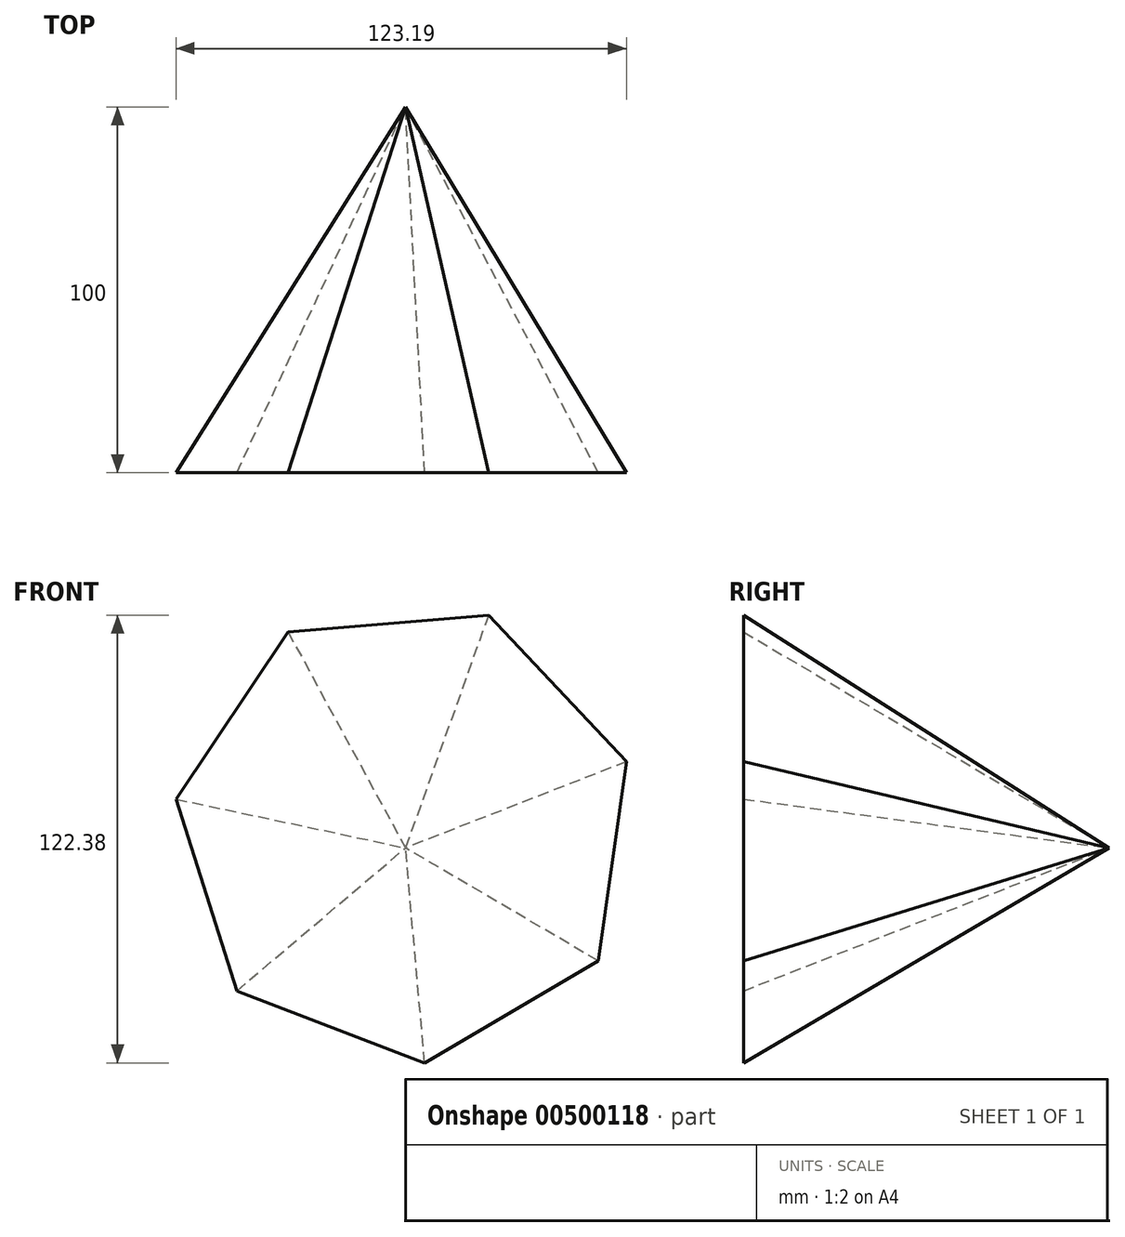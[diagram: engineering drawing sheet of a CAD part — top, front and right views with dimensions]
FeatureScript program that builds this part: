
annotation { "Feature Type Name" : "Feature", "Feature Type Description" : "" }
export const myFeature = defineFeature(function(context is Context, id is Id, definition is map)
    precondition{}
    {
        {
            var Q0;
            Q0=qCreatedBy(makeId("Front.planeOp"),FACE);
            var sketch = newSketch(context, id + "F0", { "sketchPlane" : qUnion([Q0])});
            skCircle(sketch, "E0.cCircle", {"center": v(0, 0) * mm, "radius": 63.4 * mm, "construction": true});
            skLineSegment(sketch, "E0.0", {"start": v(-32.13, 54.65) * mm, "end": v(22.7, 59.2) * mm});
            skLineSegment(sketch, "E0.1", {"start": v(22.7, 59.2) * mm, "end": v(60.43, 19.16) * mm});
            skLineSegment(sketch, "E0.2", {"start": v(60.43, 19.16) * mm, "end": v(52.66, -35.3) * mm});
            skLineSegment(sketch, "E0.3", {"start": v(52.66, -35.3) * mm, "end": v(5.24, -63.18) * mm});
            skLineSegment(sketch, "E0.4", {"start": v(5.24, -63.18) * mm, "end": v(-46.13, -43.49) * mm});
            skLineSegment(sketch, "E0.5", {"start": v(-46.13, -43.49) * mm, "end": v(-62.76, 8.95) * mm});
            skLineSegment(sketch, "E0.6", {"start": v(-62.76, 8.95) * mm, "end": v(-32.13, 54.65) * mm});
            skSolve(sketch);
        }
        {
            var Q0;
            Q0=qCreatedBy(makeId("Front.planeOp"),FACE);
            cPlane(context, id + "F1", {"entities" : qUnion([Q0]), "cplaneType" : CPlaneType.OFFSET, "offset" : 100 * mm, "oppositeDirection" : true, "width" : 150 * mm, "height" : 150 * mm});
        }
        {
            var Q0;
            Q0=qCreatedBy(id+"F1.planeOp",FACE);
            var sketch = newSketch(context, id + "F2", { "sketchPlane" : qUnion([Q0])});
            skPoint(sketch, "E1", {"position": v(0, -4.4) * mm});
            skSolve(sketch);
        }
        {
            var Q0;
            Q0=makeQuery(id+"F0.imprint","IMPRINT",FACE,{"disambiguationData":[TD([[makeQuery(id+"F0.imprint","IMPRINT",EDGE,{"derivedFrom":sQuery(id+"F0.wireOp",EDGE,"E0.0")}),-1.0]])]});
            var Q1;
            Q1=sQuery(id+"F2.wireOp",VERTEX,"E1");
            loft(context, id + "F3", {"sheetProfilesArray" : [{ "sheetProfileEntities" : qUnion([Q0]) }, { "sheetProfileEntities" : qUnion([Q1]) }]});
        }
    });
